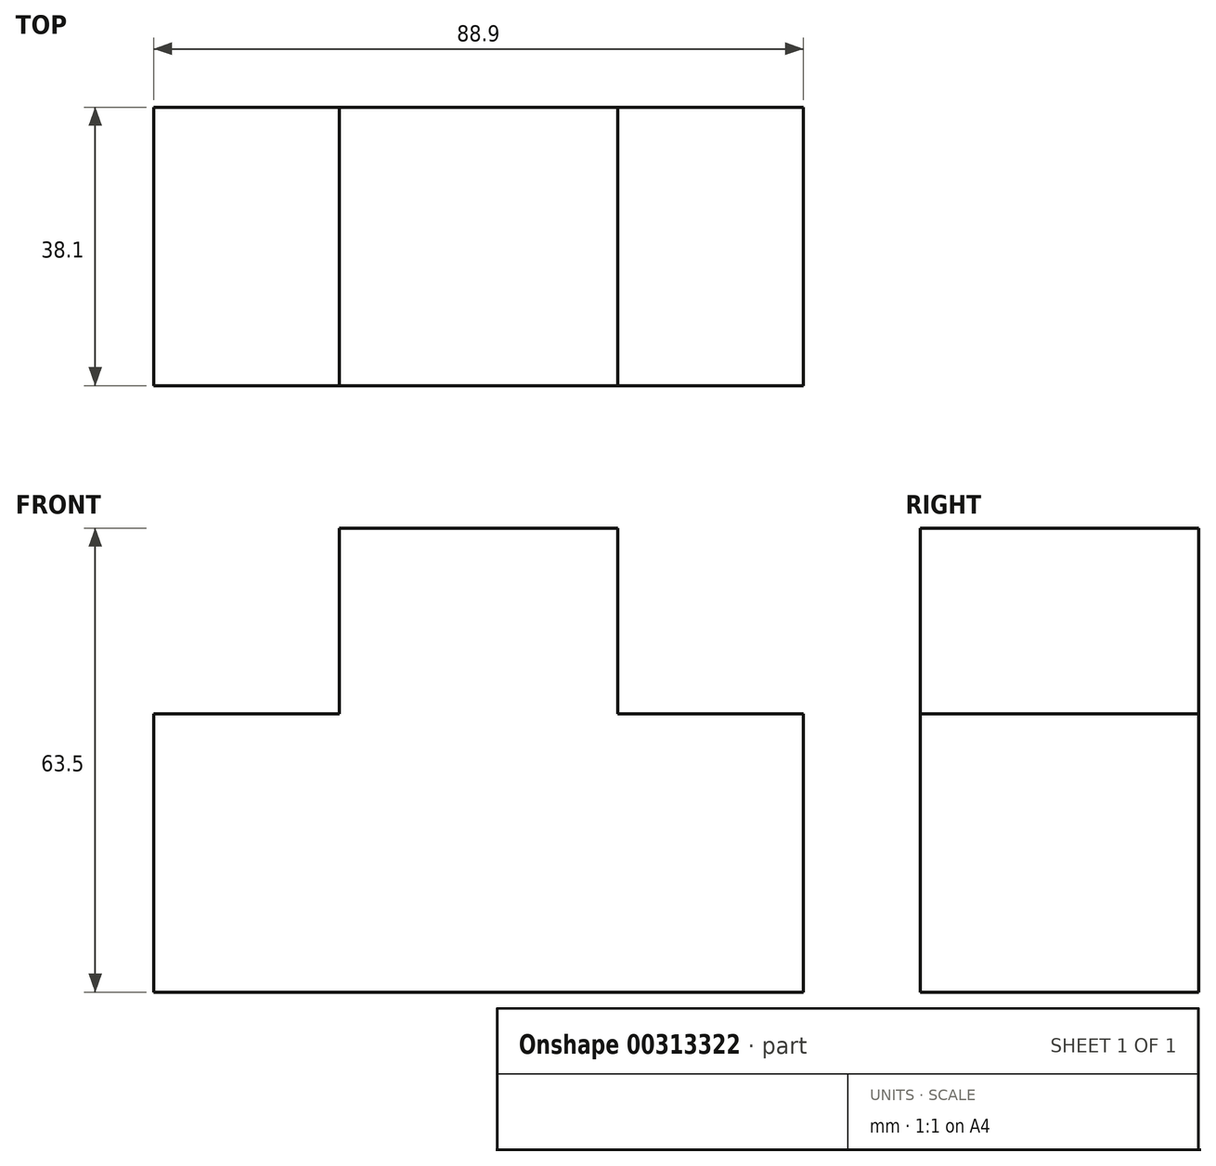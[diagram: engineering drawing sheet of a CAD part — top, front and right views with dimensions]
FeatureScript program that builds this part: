
annotation { "Feature Type Name" : "Feature", "Feature Type Description" : "" }
export const myFeature = defineFeature(function(context is Context, id is Id, definition is map)
    precondition{}
    {
        {
            var Q0;
            Q0=qCreatedBy(makeId("Front.planeOp"),FACE);
            var sketch = newSketch(context, id + "F0", { "sketchPlane" : qUnion([Q0])});
            skLineSegment(sketch, "E0", {"start": v(55, -23.72) * mm, "end": v(55, 14.38) * mm});
            skLineSegment(sketch, "E1", {"start": v(55, 14.38) * mm, "end": v(29.6, 14.38) * mm});
            skLineSegment(sketch, "E2", {"start": v(29.6, 14.38) * mm, "end": v(29.6, 39.78) * mm});
            skLineSegment(sketch, "E3", {"start": v(29.6, 39.78) * mm, "end": v(-8.5, 39.78) * mm});
            skLineSegment(sketch, "E4", {"start": v(-8.5, 39.78) * mm, "end": v(-8.5, 14.38) * mm});
            skLineSegment(sketch, "E5", {"start": v(-8.5, 14.38) * mm, "end": v(-33.9, 14.38) * mm});
            skLineSegment(sketch, "E6", {"start": v(-33.9, 14.38) * mm, "end": v(-33.9, -23.72) * mm});
            skLineSegment(sketch, "E7", {"start": v(-33.9, -23.72) * mm, "end": v(55, -23.72) * mm});
            skSolve(sketch);
        }
        {
            var Q0;
            Q0=makeQuery(id+"F0.imprint","IMPRINT",FACE,{"disambiguationData":[TD([[makeQuery(id+"F0.imprint","IMPRINT",EDGE,{"derivedFrom":sQuery(id+"F0.wireOp",EDGE,"E0")}),1.0]])]});
            extrude(context, id + "F1", {"entities" : qUnion([Q0]), "depth" : 38.1 * mm});
        }
    });
